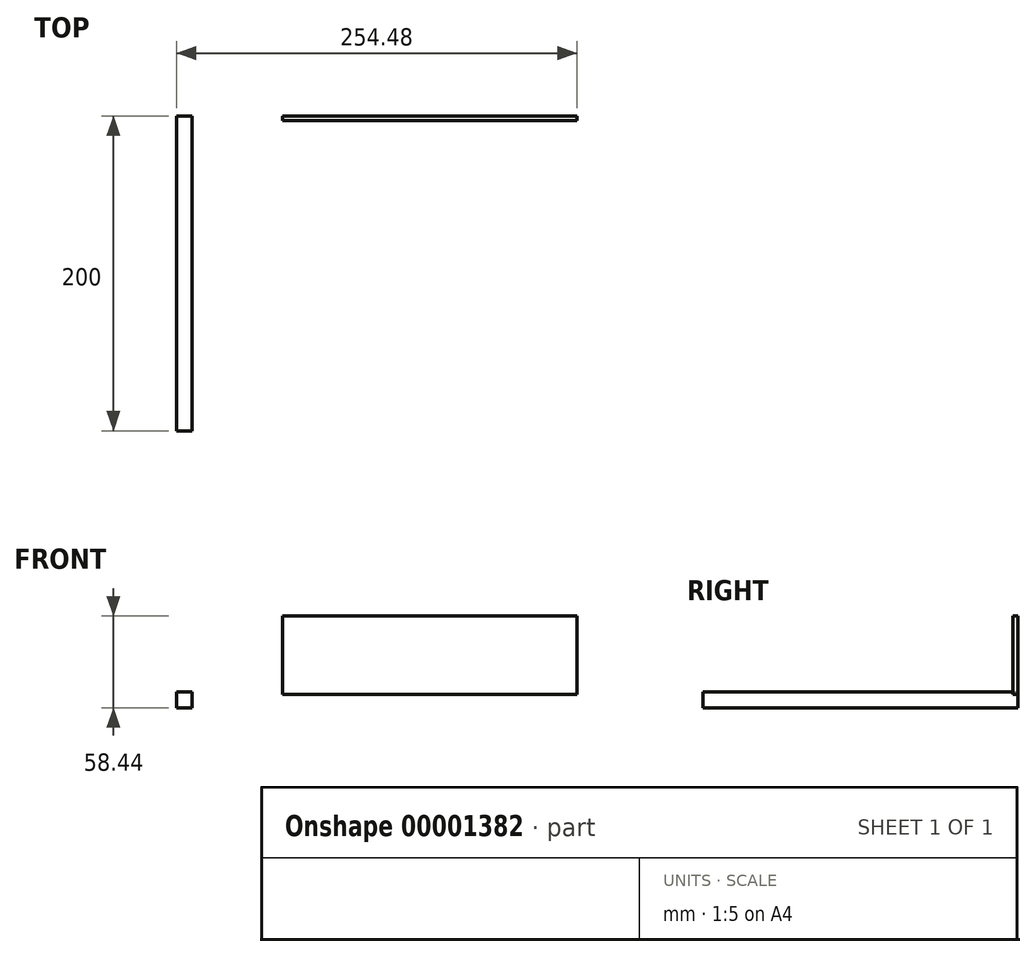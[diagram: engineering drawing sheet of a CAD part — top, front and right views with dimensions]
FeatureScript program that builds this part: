
annotation { "Feature Type Name" : "Feature", "Feature Type Description" : "" }
export const myFeature = defineFeature(function(context is Context, id is Id, definition is map)
    precondition{}
    {
        {
            var Q0;
            Q0=qCreatedBy(makeId("Front.planeOp"),FACE);
            var sketch = newSketch(context, id + "F0", { "sketchPlane" : qUnion([Q0])});
            skLineSegment(sketch, "E0.bottom", {"start": v(-109.18, 27.15) * mm, "end": v(-99.18, 27.15) * mm});
            skLineSegment(sketch, "E0.top", {"start": v(-109.18, 17.15) * mm, "end": v(-99.18, 17.15) * mm});
            skLineSegment(sketch, "E0.left", {"start": v(-109.18, 27.15) * mm, "end": v(-109.18, 17.15) * mm});
            skLineSegment(sketch, "E0.right", {"start": v(-99.18, 27.15) * mm, "end": v(-99.18, 17.15) * mm});
            skSolve(sketch);
        }
        {
            var Q0;
            Q0 = qSketchRegion(id + "F0", true);
            extrude(context, id + "F1", {"entities" : qUnion([Q0]), "depth" : 200 * mm});
        }
        {
            var Q0;
            Q0=qCreatedBy(makeId("Front.planeOp"),FACE);
            var sketch = newSketch(context, id + "F2", { "sketchPlane" : qUnion([Q0])});
            skLineSegment(sketch, "E1.bottom", {"start": v(-41.7, 25.59) * mm, "end": v(145.3, 25.59) * mm});
            skLineSegment(sketch, "E1.top", {"start": v(-41.7, 75.59) * mm, "end": v(145.3, 75.59) * mm});
            skLineSegment(sketch, "E1.left", {"start": v(-41.7, 25.59) * mm, "end": v(-41.7, 75.59) * mm});
            skLineSegment(sketch, "E1.right", {"start": v(145.3, 25.59) * mm, "end": v(145.3, 75.59) * mm});
            skSolve(sketch);
        }
        {
            var Q0;
            Q0 = qSketchRegion(id + "F2", true);
            extrude(context, id + "F3", {"entities" : qUnion([Q0]), "depth" : 3 * mm});
        }
    });
